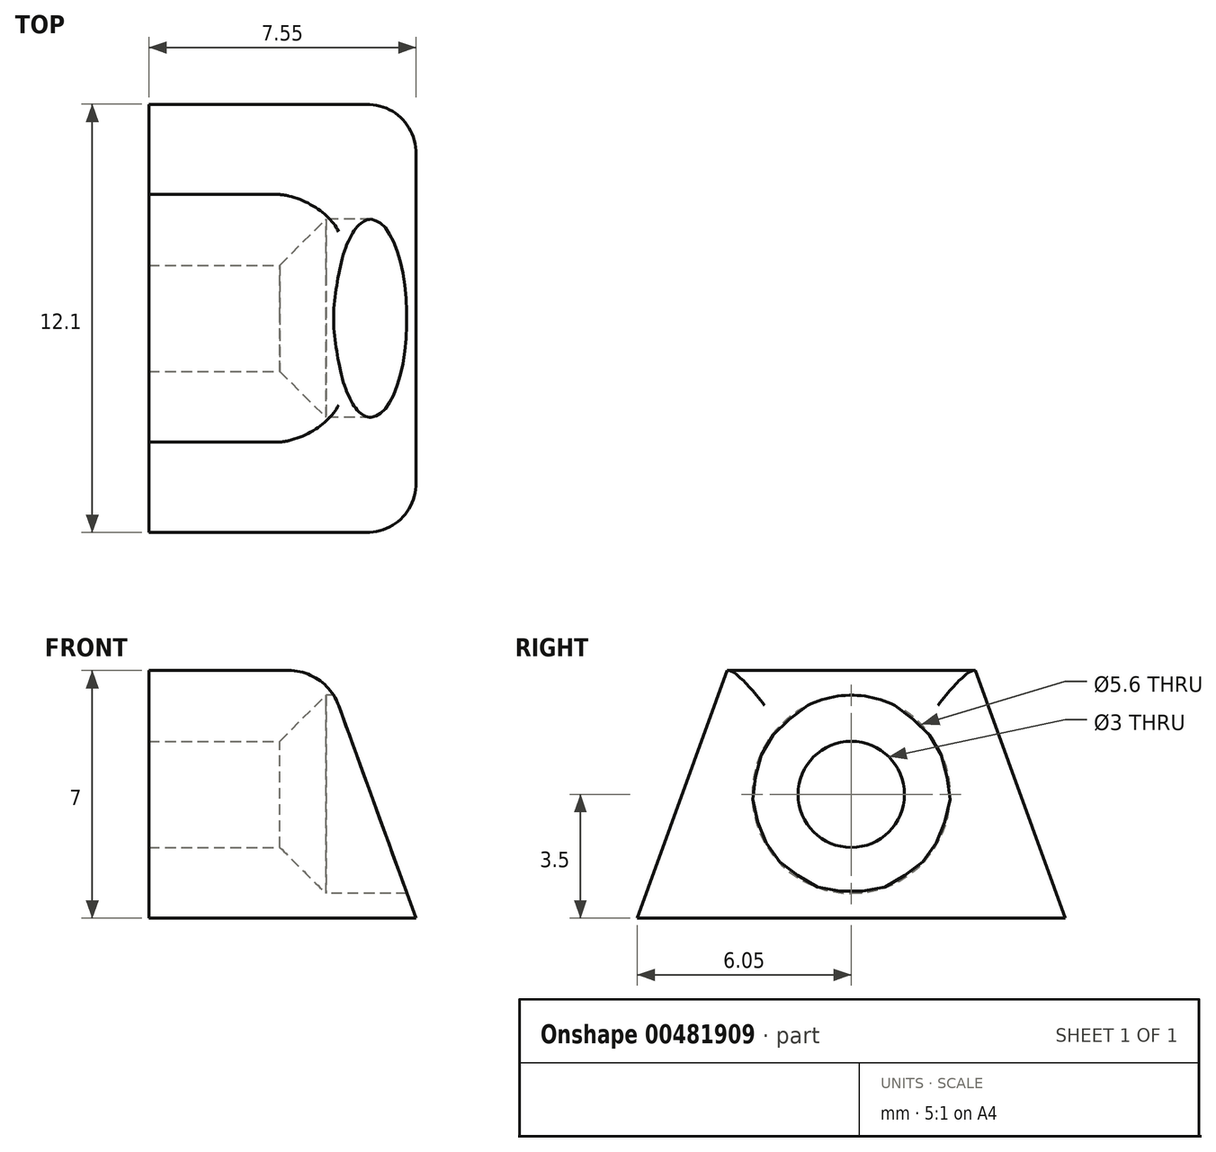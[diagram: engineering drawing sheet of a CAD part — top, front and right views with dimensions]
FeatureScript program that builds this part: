
annotation { "Feature Type Name" : "Feature", "Feature Type Description" : "" }
export const myFeature = defineFeature(function(context is Context, id is Id, definition is map)
    precondition{}
    {
        {
            var Q0;
            Q0=qCreatedBy(makeId("Front.planeOp"),FACE);
            var sketch = newSketch(context, id + "F0", { "sketchPlane" : qUnion([Q0])});
            skLineSegment(sketch, "E0", {"start": v(0, 0) * mm, "end": v(7.55, 0) * mm});
            skLineSegment(sketch, "E1", {"start": v(7.55, 0) * mm, "end": v(5, 7) * mm});
            skLineSegment(sketch, "E2", {"start": v(5, 7) * mm, "end": v(0, 7) * mm});
            skLineSegment(sketch, "E3", {"start": v(0, 7) * mm, "end": v(0, 0) * mm});
            skSolve(sketch);
        }
        {
            var Q0;
            Q0=makeQuery(id+"F0.imprint","IMPRINT",FACE,{"disambiguationData":[TD([[makeQuery(id+"F0.imprint","IMPRINT",EDGE,{"derivedFrom":sQuery(id+"F0.wireOp",EDGE,"E0")}),1.0]])]});
            extrude(context, id + "F1", {"entities" : qUnion([Q0]), "endBound" : BoundingType.SYMMETRIC, "depth" : 15 * mm});
        }
        {
            var Q0;
            Q0=makeQuery(id+"F1.opExtrude","SWEPT_FACE",FACE,{"disambiguationData":[OSD([sQuery(id+"F0.wireOp",EDGE,"E3")])]});
            var sketch = newSketch(context, id + "F2", { "sketchPlane" : qUnion([Q0])});
            skLineSegment(sketch, "E4", {"start": v(-6.05, 0) * mm, "end": v(6.05, 0) * mm});
            skLineSegment(sketch, "E5", {"start": v(6.05, 0) * mm, "end": v(3.5, 7) * mm});
            skLineSegment(sketch, "E6", {"start": v(3.5, 7) * mm, "end": v(-3.5, 7) * mm});
            skLineSegment(sketch, "E7", {"start": v(-3.5, 7) * mm, "end": v(-6.05, 0) * mm});
            skPoint(sketch, "E8", {"position": v(0, 7) * mm});
            skSolve(sketch);
        }
        {
            var Q0;
            Q0=makeQuery(id+"F2.imprint","IMPRINT",FACE,{"disambiguationData":[TD([[makeQuery(id+"F2.imprint","IMPRINT",EDGE,{"derivedFrom":sQuery(id+"F2.wireOp",EDGE,"E4")}),-1.0]])]});
            extrude(context, id + "F3", {"entities" : qUnion([Q0]), "oppositeDirection" : true, "depth" : 25 * mm});
        }
        {
            var Q0;
            Q0=makeQuery(id+"F1.opExtrude","SWEPT_BODY",BODY,{"disambiguationData":[OSD([sQuery(id+"F0.wireOp",EDGE,"E0"),sQuery(id+"F0.wireOp",EDGE,"E1"),sQuery(id+"F0.wireOp",EDGE,"E2"),sQuery(id+"F0.wireOp",EDGE,"E3")])]});
            var Q1;
            Q1=makeQuery(id+"F3.opExtrude","SWEPT_BODY",BODY,{"disambiguationData":[OSD([sQuery(id+"F2.wireOp",EDGE,"E4"),sQuery(id+"F2.wireOp",EDGE,"E5"),sQuery(id+"F2.wireOp",EDGE,"E6"),sQuery(id+"F2.wireOp",EDGE,"E7")])]});
            booleanBodies(context, id + "F4", {"operationType" : BooleanOperationType.INTERSECTION, "tools" : qUnion([Q0, Q1])});
        }
        {
            var Q0;
            Q0=makeQuery(id+"F1.opExtrude","SWEPT_FACE",FACE,{"disambiguationData":[OSD([sQuery(id+"F0.wireOp",EDGE,"E3")])]});
            cPlane(context, id + "F5", {"entities" : qUnion([Q0]), "cplaneType" : CPlaneType.OFFSET, "offset" : 5 * mm, "oppositeDirection" : true, "width" : 150 * mm, "height" : 150 * mm});
        }
        {
            var Q0;
            Q0=qCreatedBy(id+"F5.planeOp",FACE);
            var sketch = newSketch(context, id + "F6", { "sketchPlane" : qUnion([Q0])});
            skPoint(sketch, "E9", {"position": v(0, 3.5) * mm});
            skSolve(sketch);
        }
        {
            var Q0;
            Q0=sQuery(id+"F6.wireOp",VERTEX,"E9");
            var Q1;
            Q1=makeQuery(id+"F4.opBoolean","INTERSECT",BODY,{"derivedFrom":[makeQuery(id+"F1.opExtrude","SWEPT_BODY",BODY,{"disambiguationData":[OSD([sQuery(id+"F0.wireOp",EDGE,"E0"),sQuery(id+"F0.wireOp",EDGE,"E1"),sQuery(id+"F0.wireOp",EDGE,"E2"),sQuery(id+"F0.wireOp",EDGE,"E3")])]}),makeQuery(id+"F3.opExtrude","SWEPT_BODY",BODY,{"disambiguationData":[OSD([sQuery(id+"F2.wireOp",EDGE,"E4"),sQuery(id+"F2.wireOp",EDGE,"E5"),sQuery(id+"F2.wireOp",EDGE,"E6"),sQuery(id+"F2.wireOp",EDGE,"E7")])]})]});
            hole(context, id + "F7", {"style" : HoleStyle.SIMPLE, "endStyle" : HoleEndStyle.THROUGH, "holeDiameter" : 5.6 * mm, "isTappedThrough" : true, "tappedDepth" : 12 * mm, "tapClearance" : 3, "locations" : qUnion([Q0]), "scope" : qUnion([Q1])});
        }
        {
            var Q0;
            Q0=sQuery(id+"F6.wireOp",VERTEX,"E9");
            var Q1;
            Q1=makeQuery(id+"F4.opBoolean","INTERSECT",BODY,{"derivedFrom":[makeQuery(id+"F1.opExtrude","SWEPT_BODY",BODY,{"disambiguationData":[OSD([sQuery(id+"F0.wireOp",EDGE,"E0"),sQuery(id+"F0.wireOp",EDGE,"E1"),sQuery(id+"F0.wireOp",EDGE,"E2"),sQuery(id+"F0.wireOp",EDGE,"E3")])]}),makeQuery(id+"F3.opExtrude","SWEPT_BODY",BODY,{"disambiguationData":[OSD([sQuery(id+"F2.wireOp",EDGE,"E4"),sQuery(id+"F2.wireOp",EDGE,"E5"),sQuery(id+"F2.wireOp",EDGE,"E6"),sQuery(id+"F2.wireOp",EDGE,"E7")])]})]});
            hole(context, id + "F8", {"style" : HoleStyle.C_SINK, "endStyle" : HoleEndStyle.THROUGH, "oppositeDirection" : true, "holeDiameter" : 3 * mm, "cSinkDiameter" : 5.6 * mm, "cSinkAngle" : 90 * degree, "isTappedThrough" : true, "tappedDepth" : 12 * mm, "tapClearance" : 3, "locations" : qUnion([Q0]), "scope" : qUnion([Q1])});
        }
        {
            var Q0;
            Q0=makeQuery(id+"F4.opBoolean","INTERSECT",EDGE,{"derivedFrom":[makeQuery(id+"F1.opExtrude","SWEPT_FACE",FACE,{"disambiguationData":[OSD([sQuery(id+"F0.wireOp",EDGE,"E1")])]}),makeQuery(id+"F3.opExtrude","SWEPT_FACE",FACE,{"disambiguationData":[OSD([sQuery(id+"F2.wireOp",EDGE,"E7")])]})]});
            var Q1;
            Q1=makeQuery(id+"F4.opBoolean","INTERSECT",EDGE,{"derivedFrom":[makeQuery(id+"F1.opExtrude","SWEPT_FACE",FACE,{"disambiguationData":[OSD([sQuery(id+"F0.wireOp",EDGE,"E1")])]}),makeQuery(id+"F3.opExtrude","SWEPT_FACE",FACE,{"disambiguationData":[OSD([sQuery(id+"F2.wireOp",EDGE,"E5")])]})]});
            var Q2;
            Q2=makeQuery(id+"F3.opExtrude","SWEPT_EDGE",EDGE,{"disambiguationData":[OSD([sQuery(id+"F0.wireOp",EDGE,"E2"),sQuery(id+"F0.wireOp",EDGE,"E3"),sQuery(id+"F2.wireOp",EDGE,"E5"),sQuery(id+"F2.wireOp",EDGE,"E6")])]});
            var Q3;
            Q3=makeQuery(id+"F3.opExtrude","SWEPT_EDGE",EDGE,{"disambiguationData":[OSD([sQuery(id+"F0.wireOp",EDGE,"E2"),sQuery(id+"F0.wireOp",EDGE,"E3"),sQuery(id+"F2.wireOp",EDGE,"E6"),sQuery(id+"F2.wireOp",EDGE,"E7")])]});
            var Q4;
            Q4=makeQuery(id+"F1.opExtrude","SWEPT_EDGE",EDGE,{"disambiguationData":[OSD([sQuery(id+"F0.wireOp",EDGE,"E1"),sQuery(id+"F0.wireOp",EDGE,"E2")])]});
            fillet(context, id + "F9", {"entities" : qUnion([Q0, Q1, Q2, Q3, Q4]), "radius" : 1.5 * mm, "tangentPropagation" : true, "allowEdgeOverflow" : false});
        }
    });
